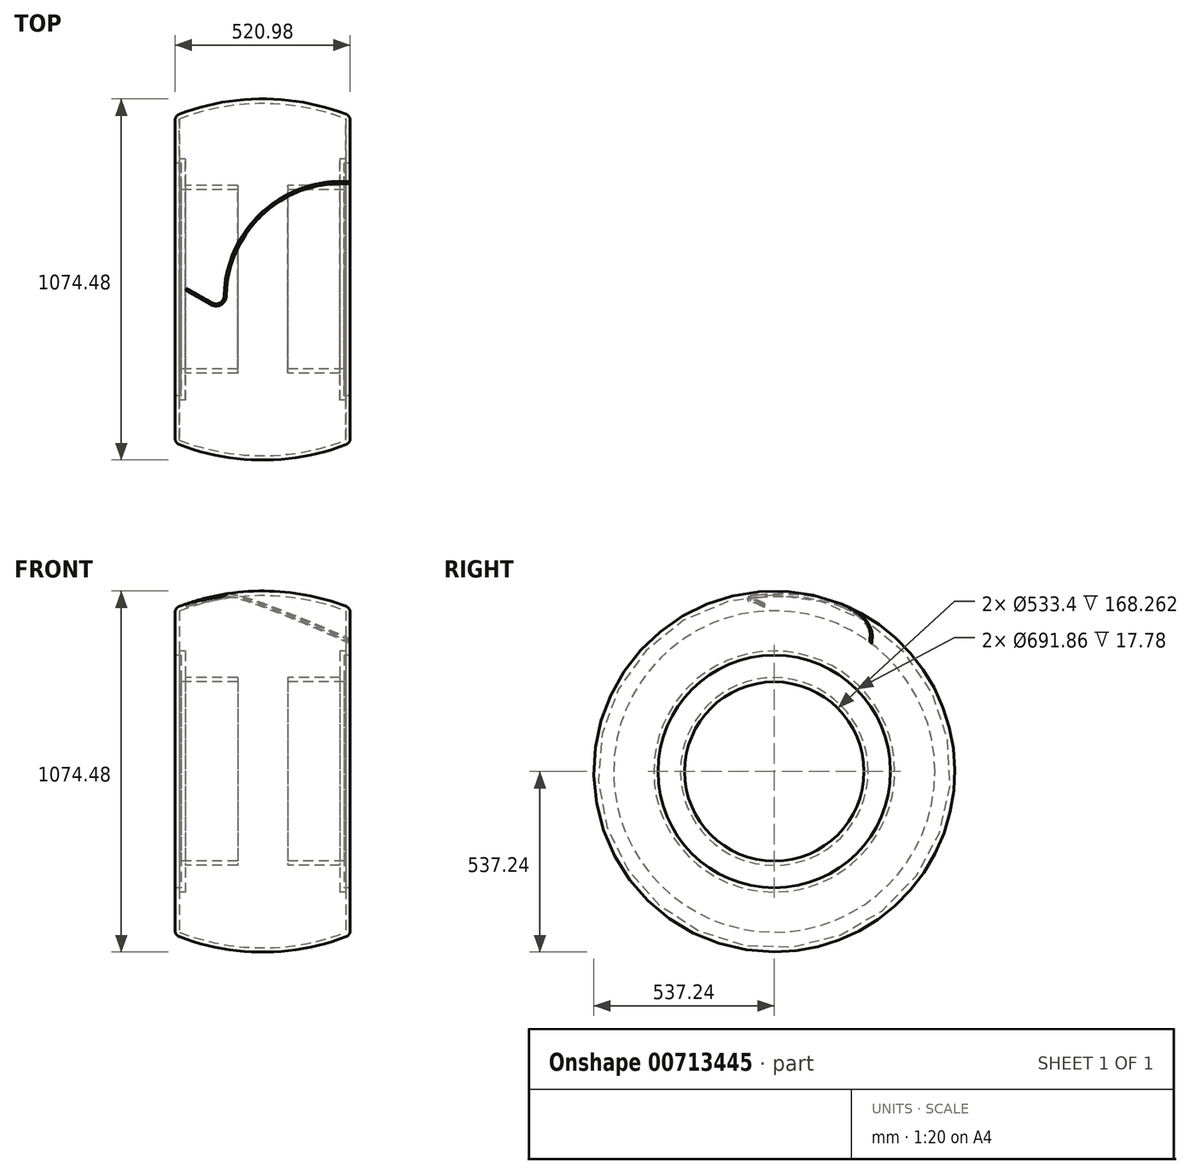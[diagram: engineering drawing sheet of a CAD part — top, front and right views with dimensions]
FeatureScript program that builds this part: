
annotation { "Feature Type Name" : "Feature", "Feature Type Description" : "" }
export const myFeature = defineFeature(function(context is Context, id is Id, definition is map)
    precondition{}
    {
        {
            var Q0;
            Q0=qCreatedBy(makeId("Front.planeOp"),FACE);
            var sketch = newSketch(context, id + "F0", { "sketchPlane" : qUnion([Q0])});
            skLineSegment(sketch, "E0", {"start": v(0, 428.57) * mm, "end": v(0, -398.15) * mm});
            skLineSegment(sketch, "E1", {"start": v(-651.94, 0) * mm, "end": v(606.63, 0) * mm});
            skLineSegment(sketch, "E2.MirrorCS", {"start": v(-292.42, -770.57) * mm, "end": v(-241.05, -770.57) * mm});
            skLineSegment(sketch, "E3", {"start": v(-74.44, 266.7) * mm, "end": v(-242.7, 266.7) * mm});
            skLineSegment(sketch, "E4", {"start": v(-242.7, 345.93) * mm, "end": v(-242.7, 266.7) * mm});
            skLineSegment(sketch, "E5", {"start": v(-242.7, 345.93) * mm, "end": v(-260.49, 345.93) * mm});
            skLineSegment(sketch, "E6", {"start": v(-260.49, 345.93) * mm, "end": v(-260.49, 486.8) * mm});
            skLineSegment(sketch, "E7.MirrorCS", {"start": v(260.49, 345.93) * mm, "end": v(260.49, 486.8) * mm});
            skLineSegment(sketch, "E8.MirrorCS", {"start": v(242.7, 345.93) * mm, "end": v(260.49, 345.93) * mm});
            skLineSegment(sketch, "E9.MirrorCS", {"start": v(242.7, 345.93) * mm, "end": v(242.7, 266.7) * mm});
            skLineSegment(sketch, "E10.MirrorCS", {"start": v(74.44, 266.7) * mm, "end": v(242.7, 266.7) * mm});
            skArc(sketch, "E11", {"start": v(260.49, 486.8) * mm, "mid": v(0, 537.24) * mm, "end": v(-260.49, 486.8) * mm});
            skLineSegment(sketch, "E12.0", {"start": v(74.44, 279.4) * mm, "end": v(230, 279.4) * mm});
            skLineSegment(sketch, "E12.1", {"start": v(230, 358.63) * mm, "end": v(230, 279.4) * mm});
            skLineSegment(sketch, "E12.2", {"start": v(230, 358.63) * mm, "end": v(247.79, 358.63) * mm});
            skLineSegment(sketch, "E12.3", {"start": v(247.79, 358.63) * mm, "end": v(247.79, 478.16) * mm});
            skArc(sketch, "E12.4", {"start": v(247.79, 478.16) * mm, "mid": v(0, 524.54) * mm, "end": v(-247.79, 478.16) * mm});
            skLineSegment(sketch, "E12.5", {"start": v(-74.44, 279.4) * mm, "end": v(-230, 279.4) * mm});
            skLineSegment(sketch, "E12.6", {"start": v(-230, 358.63) * mm, "end": v(-230, 279.4) * mm});
            skLineSegment(sketch, "E12.7", {"start": v(-230, 358.63) * mm, "end": v(-247.79, 358.63) * mm});
            skLineSegment(sketch, "E12.8", {"start": v(-247.79, 358.63) * mm, "end": v(-247.79, 478.16) * mm});
            skLineSegment(sketch, "E13", {"start": v(-74.44, 279.4) * mm, "end": v(-74.44, 266.7) * mm});
            skLineSegment(sketch, "E14", {"start": v(74.44, 279.4) * mm, "end": v(74.44, 266.7) * mm});
            skSolve(sketch);
        }
        {
            var Q0;
            Q0=makeQuery(id+"F0.imprint","IMPRINT",FACE,{"disambiguationData":[TD([[makeQuery(id+"F0.imprint","IMPRINT",EDGE,{"derivedFrom":sQuery(id+"F0.wireOp",EDGE,"E3")}),-1.0]])]});
            var Q1;
            Q1=sQuery(id+"F0.wireOp",EDGE,"E1");
            revolve(context, id + "F1", {"surfaceOperationType" : NewSurfaceOperationType.NEW, "entities" : qUnion([Q0]), "axis" : qUnion([Q1]), "revolveType" : RevolveType.FULL});
        }
        {
            var Q0;
            Q0=makeQuery(id+"F1.opRevolve","SWEPT_EDGE",EDGE,{"disambiguationData":[OSD([sQuery(id+"F0.wireOp",EDGE,"E7.MirrorCS"),sQuery(id+"F0.wireOp",EDGE,"E11")])]});
            var Q1;
            Q1=makeQuery(id+"F1.opRevolve","SWEPT_EDGE",EDGE,{"disambiguationData":[OSD([sQuery(id+"F0.wireOp",EDGE,"E6"),sQuery(id+"F0.wireOp",EDGE,"E11")])]});
            fillet(context, id + "F2", {"entities" : qUnion([Q0, Q1]), "radius" : 19.05 * mm, "tangentPropagation" : true, "allowEdgeOverflow" : false});
        }
        {
            var Q0;
            Q0=qCreatedBy(makeId("Front.planeOp"),FACE);
            var sketch = newSketch(context, id + "F3", { "sketchPlane" : qUnion([Q0])});
            skArc(sketch, "E15.0", {"start": v(260.84, 478.7) * mm, "mid": v(-0.15, 529.87) * mm, "end": v(-261.13, 478.58) * mm});
            skSolve(sketch);
        }
        {
            var Q0;
            Q0=sQuery(id+"F3.wireOp",EDGE,"E15.0");
            var Q1;
            Q1=sQuery(id+"F0.wireOp",EDGE,"E1");
            revolve(context, id + "F4", {"bodyType" : ToolBodyType.SURFACE, "surfaceOperationType" : NewSurfaceOperationType.NEW, "surfaceEntities" : qUnion([Q0]), "axis" : qUnion([Q1]), "revolveType" : RevolveType.TWO_DIRECTIONS, "angle" : 45 * degree, "angleBack" : 315 * degree});
        }
        {
            var Q0;
            Q0=qCreatedBy(makeId("Top.planeOp"),FACE);
            cPlane(context, id + "F5", {"entities" : qUnion([Q0]), "cplaneType" : CPlaneType.OFFSET, "offset" : 556.26 * mm, "width" : 152.4 * mm, "height" : 152.4 * mm});
        }
        {
            var Q0;
            Q0=qCreatedBy(id+"F5.planeOp",FACE);
            var sketch = newSketch(context, id + "F6", { "sketchPlane" : qUnion([Q0])});
            skLineSegment(sketch, "E16", {"start": v(-260.49, -473.8) * mm, "end": v(-260.49, 473.8) * mm});
            skLineSegment(sketch, "E17", {"start": v(260.49, -473.8) * mm, "end": v(260.49, 473.8) * mm});
            skSolve(sketch);
        }
        {
            var Q0;
            Q0=qCreatedBy(id+"F5.planeOp",FACE);
            var sketch = newSketch(context, id + "F7", { "sketchPlane" : qUnion([Q0])});
            skLineSegment(sketch, "E18", {"start": v(-725.66, 0) * mm, "end": v(688.83, 0) * mm});
            skArc(sketch, "E19", {"start": v(260.49, 284.37) * mm, "mid": v(4.06, 196.67) * mm, "end": v(-108.56, -49.84) * mm});
            skArc(sketch, "E20", {"start": v(-153.35, -75.33) * mm, "mid": v(-123.73, -75.28) * mm, "end": v(-108.56, -49.84) * mm});
            skLineSegment(sketch, "E21", {"start": v(-153.35, -75.33) * mm, "end": v(-226.5, -34.03) * mm});
            skArc(sketch, "E22.0", {"start": v(260.49, 290.74) * mm, "mid": v(-0.39, 201.21) * mm, "end": v(-114.9, -49.7) * mm});
            skArc(sketch, "E22.1", {"start": v(-150.23, -69.8) * mm, "mid": v(-126.87, -69.76) * mm, "end": v(-114.9, -49.7) * mm});
            skLineSegment(sketch, "E22.2", {"start": v(-150.23, -69.8) * mm, "end": v(-223.38, -28.5) * mm});
            skArc(sketch, "E23", {"start": v(-223.38, -28.5) * mm, "mid": v(-227.7, -29.7) * mm, "end": v(-226.5, -34.03) * mm});
            skLineSegment(sketch, "E24.0", {"start": v(260.49, -473.8) * mm, "end": v(260.49, 473.8) * mm});
            skSolve(sketch);
        }
        {
            var Q0;
            {var subQ0=sQuery(id+"F7.wireOp",EDGE,"E22.0");var subQ1=sQuery(id+"F7.wireOp",EDGE,"E18");var subQ2=makeQuery(id+"F7.imprint","INTERSECT",VERTEX,{"derivedFrom":[subQ1,subQ0]});Q0=makeQuery(id+"F7.imprint","IMPRINT",FACE,{"disambiguationData":[TD([[makeQuery(id+"F7.imprint","IMPRINT",EDGE,{"disambiguationData":[TD([[subQ2,-1.0]])],"derivedFrom":subQ1}),1.0]])]});}
            var Q1;
            {var subQ0=sQuery(id+"F7.wireOp",EDGE,"E20");Q1=makeQuery(id+"F7.imprint","IMPRINT",FACE,{"disambiguationData":[TD([[makeQuery(id+"F7.imprint","IMPRINT",EDGE,{"derivedFrom":subQ0}),1.0]])]});}
            var Q2;
            Q2=makeQuery(id+"F4.opRevolve","SWEPT_FACE",FACE,{"disambiguationData":[OSD([sQuery(id+"F3.wireOp",EDGE,"E15.0")])]});
            extrude(context, id + "F8", {"entities" : qUnion([Q0, Q1]), "operationType" : NewBodyOperationType.REMOVE, "endBound" : BoundingType.UP_TO_SURFACE, "oppositeDirection" : true, "depth" : 25.4 * mm, "endBoundEntityFace" : qUnion([Q2]), "offsetDistance" : 25.4 * mm});
        }
    });
